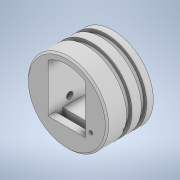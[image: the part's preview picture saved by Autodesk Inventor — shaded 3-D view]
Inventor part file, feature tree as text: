
AUTODESK INVENTOR PART (.ipt)
format: ipt  version: 2020 (Build 240168000, 168)  size: 229,888 bytes
history: native  units: in
note: dims shown in document units (in); Inventor stores cm internally (conversion verified against a paired STEP export)
features: extrude x7, sketch x7, plane x3, projected_geometry x2, direct_edit x1, chamfer x1, move_body x1
ambient origin geometry x8: Origin, YZ Plane, XZ Plane, XY Plane, X Axis, Y Axis, Z Axis, Center Point
bodies: Solid1 (feature_tree)
feature tree (22):
  extrude  "Extrusion1"  Depth=1.5in TaperAngle=0.0deg
  extrude  "Extrusion2"  Depth=1.39in
  plane  "Work Plane1"
  extrude  "Extrusion3"  TaperAngle=0.0deg  [1 undecoded]
  extrude  "Extrusion4"  Depth=0.24in
  extrude  "Extrusion5"  Depth=0.4in
  plane  "Work Plane2"
  extrude  "Extrusion6"  Depth=1.459in TaperAngle=0.0deg
  plane  "Work Plane3"
  extrude  "Extrusion7"  Depth=0.195in
  direct_edit  "Direct Edit1"
  chamfer  "Chamfer1"  Distance=0.2in
  sketch  "Sketch1"  dims[d0=2.972in d1=1.5in d2=0.0in]
  sketch  "Sketch2"  dims[d3=2.502in d4=1.39in]
  sketch  "Sketch3"  dims[d5=0.75in d6=0.0in d7=0.0in]
  projected_geometry  "Projected Loop1"
  sketch  "Sketch4"  dims[d8=0.24in d10=0.24in]
  sketch  "Sketch6"  dims[d11=0.4in d12=0.4in]
  projected_geometry  "Projected Loop2"
  sketch  "Sketch7"  dims[d13=0.26in d14=1.459in d15=0.0in]
  sketch  "Sketch8"  dims[d17=0.12in d18=0.13in d19=0.2in d20=0.0in d21=0.0in d23=0.27in d24=0.14in d25=1.486in d26=0.0in d27=-0.58in d28=0.195in d29=0.0in d30=0.11in d31=0.35in d33=0.11in d34=0.195in d35=0.0in d36=0.0in d37=0.0in d38=0.215in d39=0.0625in d40=0.125in d41=45.0deg d32=0.5in]
  move_body  "Move1"
note: 1 required parameter value undecoded (feature->parameter linkage not recoverable at this tier; creation-order binding heuristic only, values carry confidence <= 0.55)
